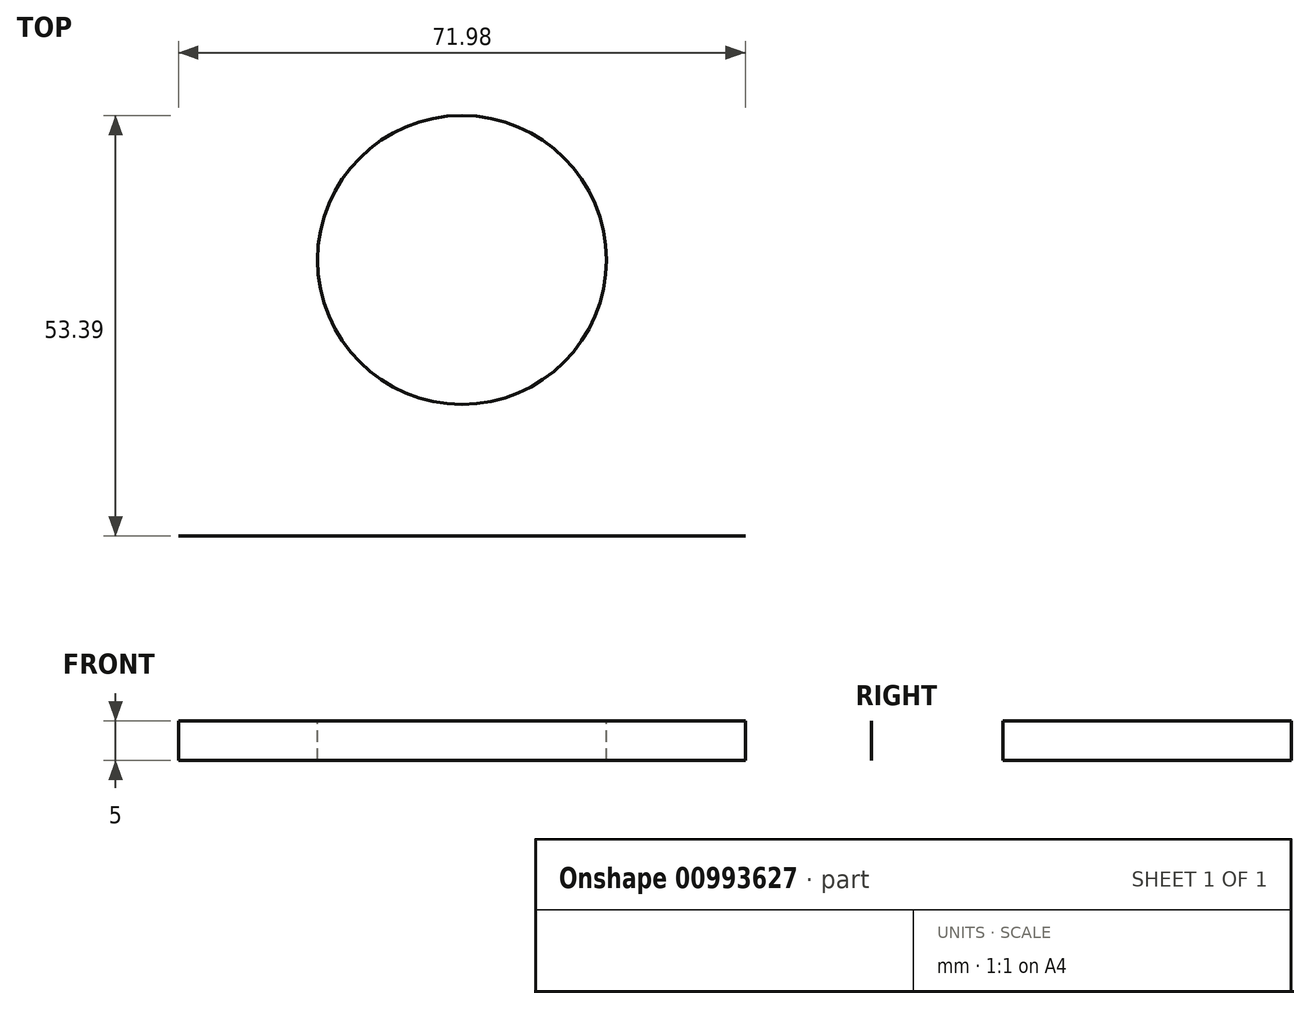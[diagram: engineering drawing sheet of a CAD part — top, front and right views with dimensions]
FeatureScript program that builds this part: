
annotation { "Feature Type Name" : "Feature", "Feature Type Description" : "" }
export const myFeature = defineFeature(function(context is Context, id is Id, definition is map)
    precondition{}
    {
        {
            var Q0;
            Q0=qCreatedBy(makeId("Top.planeOp"),FACE);
            var sketch = newSketch(context, id + "F0", { "sketchPlane" : qUnion([Q0])});
            skLineSegment(sketch, "E0.bottom", {"start": v(-36, 35.05) * mm, "end": v(36, 35.05) * mm});
            skLineSegment(sketch, "E0.top", {"start": v(-36, -35.05) * mm, "end": v(36, -35.05) * mm});
            skLineSegment(sketch, "E0.left", {"start": v(-36, 35.05) * mm, "end": v(-36, -35.05) * mm});
            skLineSegment(sketch, "E0.right", {"start": v(36, 35.05) * mm, "end": v(36, -35.05) * mm});
            skPoint(sketch, "E0.middle", {"position": v(0, 0) * mm});
            skCircle(sketch, "E1", {"center": v(0, 0) * mm, "radius": 18.34 * mm});
            skSolve(sketch);
        }
        {
            var Q0;
            Q0=sQuery(id+"F0.wireOp",EDGE,"E0.top");
            var Q1;
            Q1=sQuery(id+"F0.wireOp",EDGE,"E1");
            extrude(context, id + "F1", {"bodyType" : ToolBodyType.SURFACE, "surfaceEntities" : qUnion([Q0, Q1]), "depth" : 5 * mm, "offsetDistance" : 25 * mm});
        }
    });
